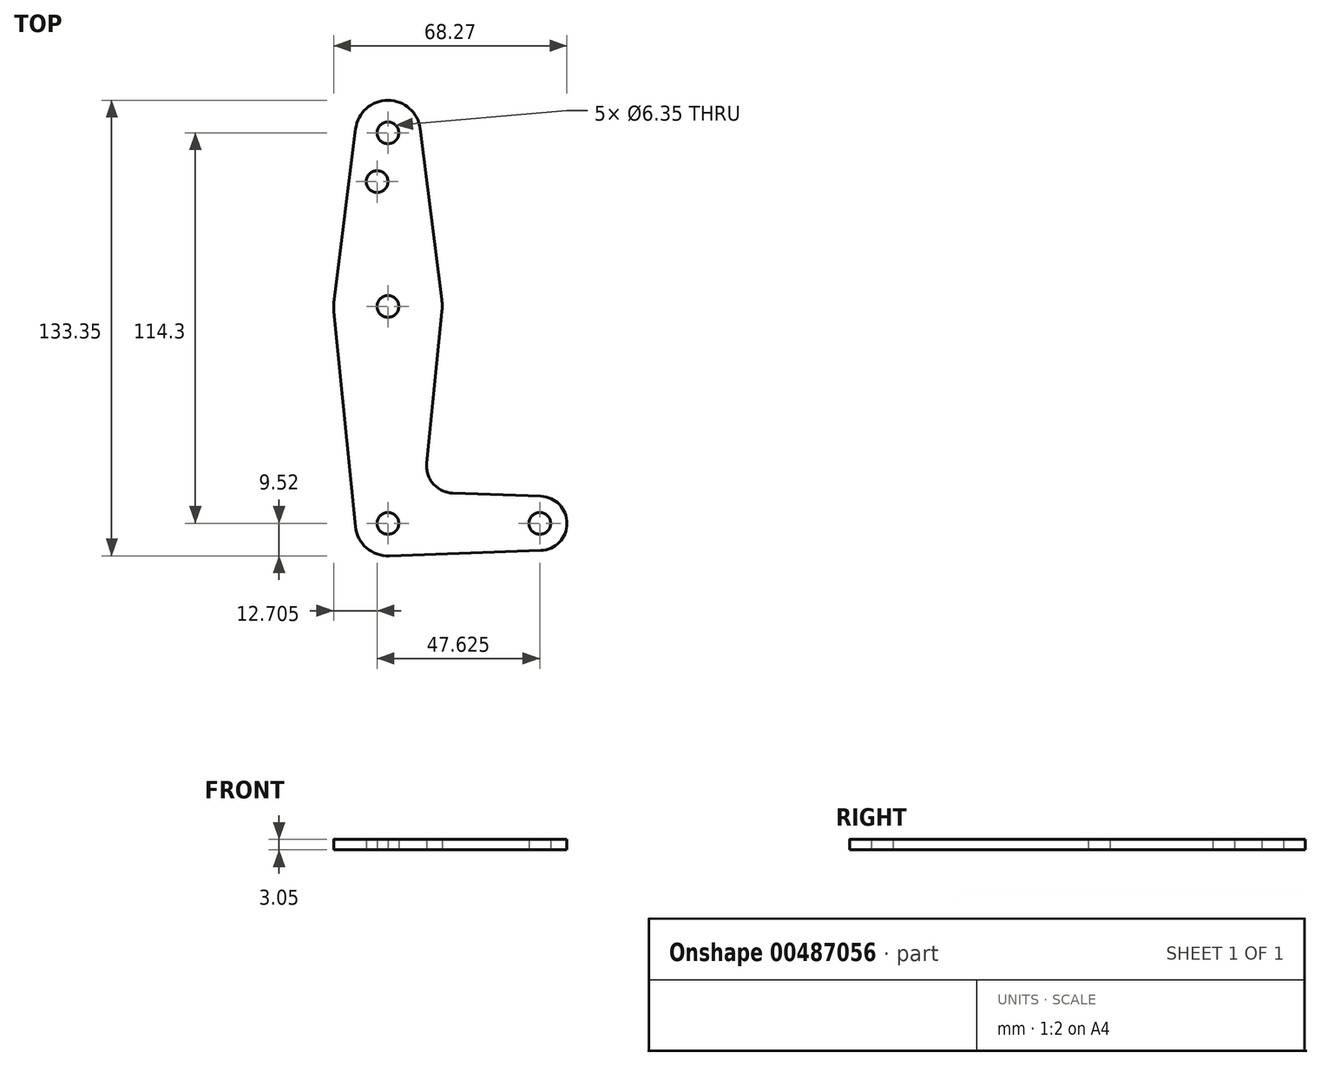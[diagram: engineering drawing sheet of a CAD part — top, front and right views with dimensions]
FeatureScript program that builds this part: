
annotation { "Feature Type Name" : "Feature", "Feature Type Description" : "" }
export const myFeature = defineFeature(function(context is Context, id is Id, definition is map)
    precondition{}
    {
        {
            var Q0;
            Q0=qCreatedBy(makeId("Top.planeOp"),FACE);
            var sketch = newSketch(context, id + "F0", { "sketchPlane" : qUnion([Q0])});
            skLineSegment(sketch, "E0", {"start": v(0, 0) * mm, "end": v(0, 114.3) * mm, "construction": true});
            skLineSegment(sketch, "E1", {"start": v(0, 0) * mm, "end": v(44.45, 0) * mm, "construction": true});
            skCircle(sketch, "E2", {"center": v(0, 0) * mm, "radius": 9.53 * mm});
            skCircle(sketch, "E3", {"center": v(0, 114.3) * mm, "radius": 9.53 * mm});
            skCircle(sketch, "E4", {"center": v(44.45, 0) * mm, "radius": 7.94 * mm});
            skCircle(sketch, "E5", {"center": v(0, 63.5) * mm, "radius": 15.88 * mm});
            skLineSegment(sketch, "E6", {"start": v(9.45, 115.5) * mm, "end": v(15.75, 65.48) * mm});
            skLineSegment(sketch, "E7", {"start": v(-9.45, 115.5) * mm, "end": v(-15.75, 65.48) * mm});
            skLineSegment(sketch, "E8", {"start": v(15.8, 61.91) * mm, "end": v(11.34, 17.6) * mm});
            skLineSegment(sketch, "E9", {"start": v(-15.8, 61.91) * mm, "end": v(-9.48, -0.95) * mm});
            skLineSegment(sketch, "E10", {"start": v(18.97, 8.85) * mm, "end": v(44.73, 7.93) * mm});
            skLineSegment(sketch, "E11", {"start": v(0.34, -9.52) * mm, "end": v(44.73, -7.93) * mm});
            skCircle(sketch, "E12", {"center": v(0, 114.3) * mm, "radius": 3.18 * mm});
            skCircle(sketch, "E13", {"center": v(-3.18, 100.03) * mm, "radius": 3.18 * mm});
            skCircle(sketch, "E14", {"center": v(0, 63.5) * mm, "radius": 3.18 * mm});
            skCircle(sketch, "E15", {"center": v(0, 0) * mm, "radius": 3.18 * mm});
            skCircle(sketch, "E16", {"center": v(44.45, 0) * mm, "radius": 3.18 * mm});
            skArc(sketch, "E17.filletArc", {"start": v(11.34, 17.6) * mm, "mid": v(13.26, 11.57) * mm, "end": v(18.97, 8.85) * mm});
            skSolve(sketch);
        }
        {
            var Q0;
            Q0=makeQuery(id+"F0.imprint","IMPRINT",FACE,{"disambiguationData":[TD([[makeQuery(id+"F0.imprint","IMPRINT",EDGE,{"derivedFrom":sQuery(id+"F0.wireOp",EDGE,"E12")}),-1.0]])]});
            var Q1;
            {var subQ0=sQuery(id+"F0.wireOp",EDGE,"E6");Q1=makeQuery(id+"F0.imprint","IMPRINT",FACE,{"disambiguationData":[TD([[makeQuery(id+"F0.imprint","IMPRINT",EDGE,{"derivedFrom":subQ0}),-1.0]])]});}
            var Q2;
            Q2=makeQuery(id+"F0.imprint","IMPRINT",FACE,{"disambiguationData":[TD([[makeQuery(id+"F0.imprint","IMPRINT",EDGE,{"derivedFrom":sQuery(id+"F0.wireOp",EDGE,"E14")}),-1.0]])]});
            var Q3;
            {var subQ0=sQuery(id+"F0.wireOp",EDGE,"E8");Q3=makeQuery(id+"F0.imprint","IMPRINT",FACE,{"disambiguationData":[TD([[makeQuery(id+"F0.imprint","IMPRINT",EDGE,{"derivedFrom":subQ0}),-1.0]])]});}
            var Q4;
            Q4=makeQuery(id+"F0.imprint","IMPRINT",FACE,{"disambiguationData":[TD([[makeQuery(id+"F0.imprint","IMPRINT",EDGE,{"derivedFrom":sQuery(id+"F0.wireOp",EDGE,"E15")}),-1.0]])]});
            var Q5;
            Q5=makeQuery(id+"F0.imprint","IMPRINT",FACE,{"disambiguationData":[TD([[makeQuery(id+"F0.imprint","IMPRINT",EDGE,{"derivedFrom":sQuery(id+"F0.wireOp",EDGE,"E16")}),-1.0]])]});
            extrude(context, id + "F1", {"entities" : qUnion([Q0, Q1, Q2, Q3, Q4, Q5]), "depth" : 3.05 * mm});
        }
    });
